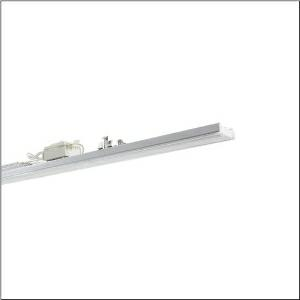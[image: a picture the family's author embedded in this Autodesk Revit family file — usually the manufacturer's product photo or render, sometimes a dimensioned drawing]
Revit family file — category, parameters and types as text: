
# Revit family: licross_r__11_recessed_mo_51te12dv4fxg3c_6e92
name_source: partatom
category: Lighting Fixtures
units: mm (PartAtom-declared; Revit-internal decimal feet)

## family parameters
Cut with Voids When Loaded = No
Host = Face
Light Source = No
Part Type = Normal
Room Calculation Point = No
Round Connector Dimension = Use Diameter
Shared = No

## types (1)
- --- (1 x LED, 1010 lm, 5.5 W, 4000K)
    Apparent Load = 6 VA
    CIE Flux Codes = 67 92 99 100 100
    Color Rendering = 80
    Color Temperature = 4000K
    Default Elevation = 1800 mm
    Description = Licross® 11 Recessed MO, luminaire insert, of sheet steel, galvanised, coil coated, white, length: 2.250mm, width: 66mm, height: 67mm, LED rated luminous flux: 15.360lm, light colour: 840, control gear: DALI 2 (for two DALI lines), with plug, 6-pole, with phase selection, for trunking rail, 14-core, mains connection: 220..240V, AC, 50/60Hz, rated input power: 88W, for trunking rail, 14-core, halogen-free wiring, for emergency light function, converter,control gear: single battery element, battery: LiFePO4, 9Ah, primary optical cover: cover, of PMMA, light emission: direct distribution, primary light characteristic: symmetric, protection rating (complete): IP54, insulation class (complete): insulation class I (protective earthing), certification: CE, UKCA, protection symbol: D if used in an environment with non-conductive dust loads with corresponding accessories, impact resistance: IK06, permissible ambient temperature for indoor applications: +5..+35°C, standard: EN 60598-2-22, LABS conformity tested according to VDMA 24364:2018-05, reducing of maximum allowable ambient temperature of 5°C with ceiling mounting, corresponds to IFS (International Featured Standards) requirements for safety and quality in the food industry, packaging unit: 1 piece
    Height = 58 mm
    Lamp = 1 x LED
    Lamp Light Flux = 1010 lm
    Lamp Power = 5.5 W
    Lamp count = 1
    Length = 2250 mm
    Luminous efficacy = 184 lm/W
    Manufacturer = Siteco
    ModVariant = No
    Model = 51TE12DV4FXG3C
    Mounting Place = Ceiling
    Mounting Type = Pendant
    Number of Poles = 1
    OnlyDefault = Yes
    Power Factor = 1
    Product Name = Licross® 11 Recessed MO
    Product group = luminaire insert
    ProductGroupID = 902
    Protection Class = Protection class I
    Protection Degree = IP 54
    RLX_Detail_Level = 1
    RLX_Emergency_Light_Flux = 0 lm
    RLX_Emergency_Type = 0
    RLX_Emergency_Type_DB = No
    RlxData = <blob elided: 29841 chars, md5=a8a5fe20>
    Socket = socket
    Standby Power = 0 W
    System Light Flux = 1010 lm
    System Power = 6 W
    Type Comments = : emergency light operation: 3 h
    Type Image = l_1296930.jpg
    URL = http://relux.com
    VarID = @adj_085278
    Voltage = 0 V
    Weight = 0.00 kg
    Width = 66 mm

## geometry (parser evidence)
native form markers: Blend x4, Sweep x8
no freeform markers — native parametric forms only
